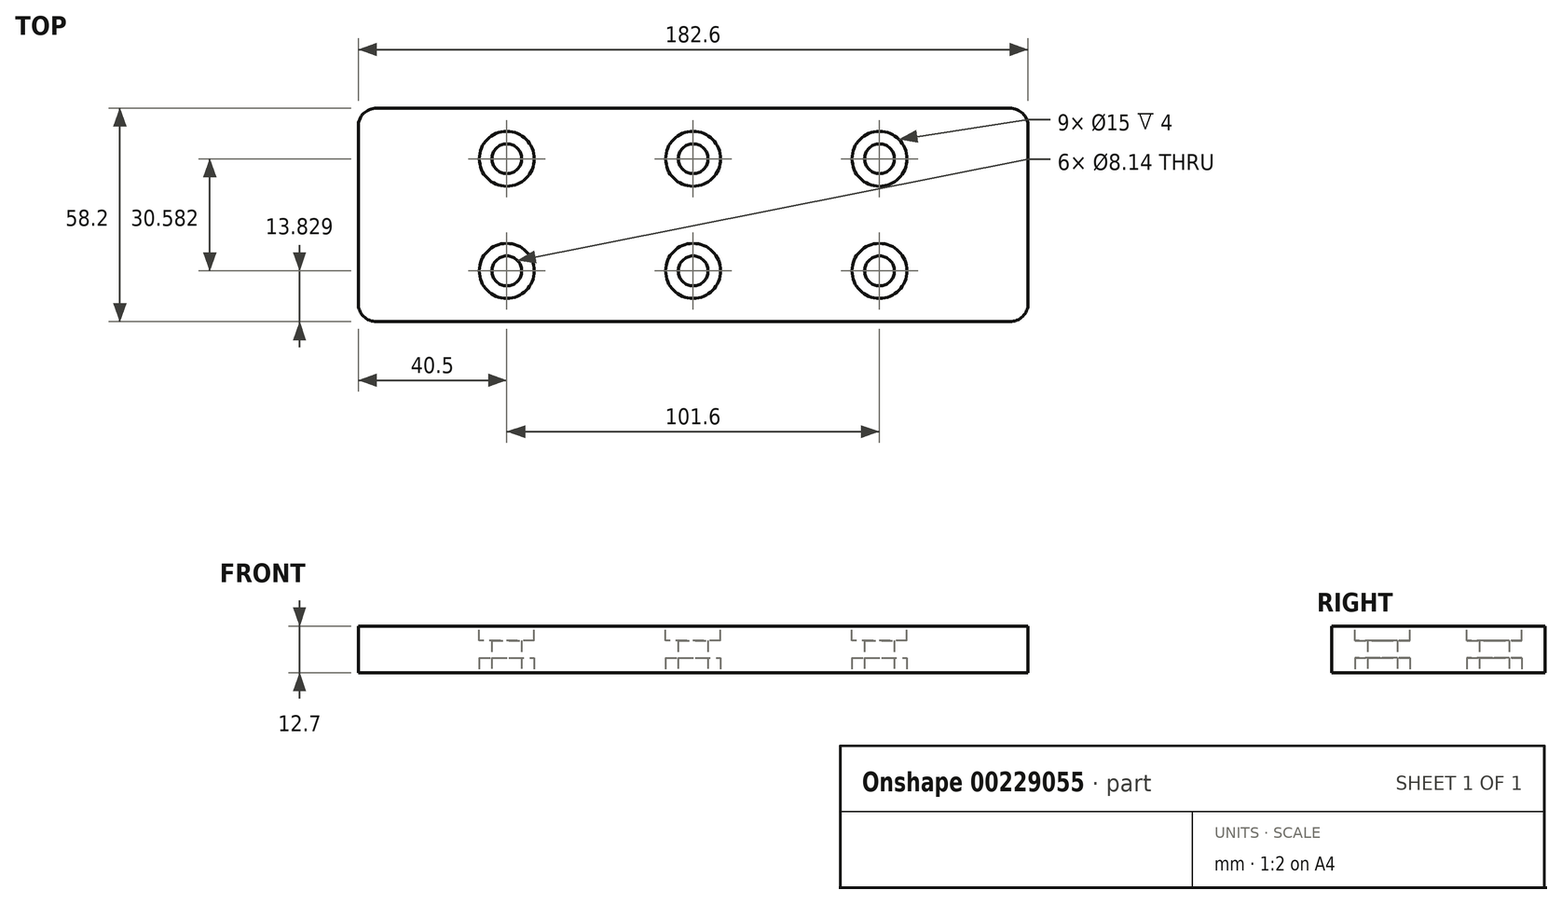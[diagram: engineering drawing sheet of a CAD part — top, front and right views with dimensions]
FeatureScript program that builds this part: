
annotation { "Feature Type Name" : "Feature", "Feature Type Description" : "" }
export const myFeature = defineFeature(function(context is Context, id is Id, definition is map)
    precondition{}
    {
        {
            assignVariable(context, id + "F0", {"name" : "counterBore", "anyValue" : 4 * mm});
        }
        {
            var Q0;
            Q0=qCreatedBy(makeId("Top.planeOp"),FACE);
            var sketch = newSketch(context, id + "F1", { "sketchPlane" : qUnion([Q0])});
            skLineSegment(sketch, "E0.bottom", {"start": v(91.3, -29.1) * mm, "end": v(-91.3, -29.1) * mm});
            skLineSegment(sketch, "E0.top", {"start": v(91.3, 29.1) * mm, "end": v(-91.3, 29.1) * mm});
            skLineSegment(sketch, "E0.left", {"start": v(91.3, -29.1) * mm, "end": v(91.3, 29.1) * mm});
            skLineSegment(sketch, "E0.right", {"start": v(-91.3, -29.1) * mm, "end": v(-91.3, 29.1) * mm});
            skSolve(sketch);
        }
        {
            var Q0;
            Q0=qCreatedBy(makeId("Top.planeOp"),FACE);
            var sketch = newSketch(context, id + "F2", { "sketchPlane" : qUnion([Q0])});
            skCircle(sketch, "E1", {"center": v(-50.8, 15.31) * mm, "radius": 4.07 * mm});
            skCircle(sketch, "E2", {"center": v(0, 15.31) * mm, "radius": 4.07 * mm});
            skCircle(sketch, "E3", {"center": v(50.8, 15.31) * mm, "radius": 4.07 * mm});
            skCircle(sketch, "E4", {"center": v(50.8, -15.27) * mm, "radius": 4.07 * mm});
            skCircle(sketch, "E5", {"center": v(0, -15.27) * mm, "radius": 4.07 * mm});
            skCircle(sketch, "E6", {"center": v(-50.8, -15.27) * mm, "radius": 4.07 * mm});
            skSolve(sketch);
        }
        {
            var Q0;
            Q0 = qSketchRegion(id + "F1", true);
            extrude(context, id + "F3", {"entities" : qUnion([Q0]), "depth" : 12.7 * mm});
        }
        {
            var Q0;
            Q0 = qSketchRegion(id + "F2", true);
            extrude(context, id + "F4", {"entities" : qUnion([Q0]), "operationType" : NewBodyOperationType.REMOVE, "endBound" : BoundingType.THROUGH_ALL, "depth" : 25 * mm});
        }
        {
            var Q0;
            Q0=makeQuery(id+"F3.opExtrude","CAP_FACE",FACE,{"disambiguationData":[OSD([sQuery(id+"F1.wireOp",EDGE,"E0.bottom"),sQuery(id+"F1.wireOp",EDGE,"E0.top"),sQuery(id+"F1.wireOp",EDGE,"E0.left"),sQuery(id+"F1.wireOp",EDGE,"E0.right")])],"isStart":false});
            var sketch = newSketch(context, id + "F5", { "sketchPlane" : qUnion([Q0])});
            skCircle(sketch, "E7", {"center": v(-50.8, 15.31) * mm, "radius": 7.5 * mm});
            skCircle(sketch, "E8", {"center": v(0, -15.27) * mm, "radius": 7.5 * mm});
            skCircle(sketch, "E9", {"center": v(50.8, 15.31) * mm, "radius": 7.5 * mm});
            skCircle(sketch, "E10", {"center": v(-50.8, -15.27) * mm, "radius": 7.5 * mm});
            skCircle(sketch, "E11", {"center": v(0, 15.31) * mm, "radius": 7.5 * mm});
            skCircle(sketch, "E12", {"center": v(50.8, -15.27) * mm, "radius": 7.5 * mm});
            skSolve(sketch);
        }
        {
            var Q0;
            Q0 = qSketchRegion(id + "F5", true);
            extrude(context, id + "F6", {"entities" : qUnion([Q0]), "operationType" : NewBodyOperationType.REMOVE, "oppositeDirection" : true, "depth" : getVariable(context, 'counterBore')});
        }
        {
            var Q0;
            Q0=makeQuery(id+"F3.opExtrude","CAP_FACE",FACE,{"disambiguationData":[OSD([sQuery(id+"F1.wireOp",EDGE,"E0.bottom"),sQuery(id+"F1.wireOp",EDGE,"E0.top"),sQuery(id+"F1.wireOp",EDGE,"E0.left"),sQuery(id+"F1.wireOp",EDGE,"E0.right")])],"isStart":true});
            var sketch = newSketch(context, id + "F7", { "sketchPlane" : qUnion([Q0])});
            skCircle(sketch, "E13", {"center": v(0, -15.31) * mm, "radius": 7.5 * mm});
            skCircle(sketch, "E14", {"center": v(-50.8, 15.27) * mm, "radius": 7.5 * mm});
            skCircle(sketch, "E15", {"center": v(50.8, 15.27) * mm, "radius": 7.5 * mm});
            skSolve(sketch);
        }
        {
            var Q0;
            Q0 = qSketchRegion(id + "F7", true);
            extrude(context, id + "F8", {"entities" : qUnion([Q0]), "operationType" : NewBodyOperationType.REMOVE, "oppositeDirection" : true, "depth" : getVariable(context, 'counterBore')});
        }
        {
            var Q0;
            Q0=makeQuery(id+"F3.opExtrude","SWEPT_EDGE",EDGE,{"disambiguationData":[OSD([sQuery(id+"F1.wireOp",EDGE,"E0.bottom"),sQuery(id+"F1.wireOp",EDGE,"E0.right")])]});
            var Q1;
            Q1=makeQuery(id+"F3.opExtrude","SWEPT_EDGE",EDGE,{"disambiguationData":[OSD([sQuery(id+"F1.wireOp",EDGE,"E0.top"),sQuery(id+"F1.wireOp",EDGE,"E0.right")])]});
            var Q2;
            Q2=makeQuery(id+"F3.opExtrude","SWEPT_EDGE",EDGE,{"disambiguationData":[OSD([sQuery(id+"F1.wireOp",EDGE,"E0.top"),sQuery(id+"F1.wireOp",EDGE,"E0.left")])]});
            var Q3;
            Q3=makeQuery(id+"F3.opExtrude","SWEPT_EDGE",EDGE,{"disambiguationData":[OSD([sQuery(id+"F1.wireOp",EDGE,"E0.bottom"),sQuery(id+"F1.wireOp",EDGE,"E0.left")])]});
            fillet(context, id + "F9", {"entities" : qUnion([Q0, Q1, Q2, Q3]), "radius" : 5 * mm, "tangentPropagation" : true, "allowEdgeOverflow" : false});
        }
    });
